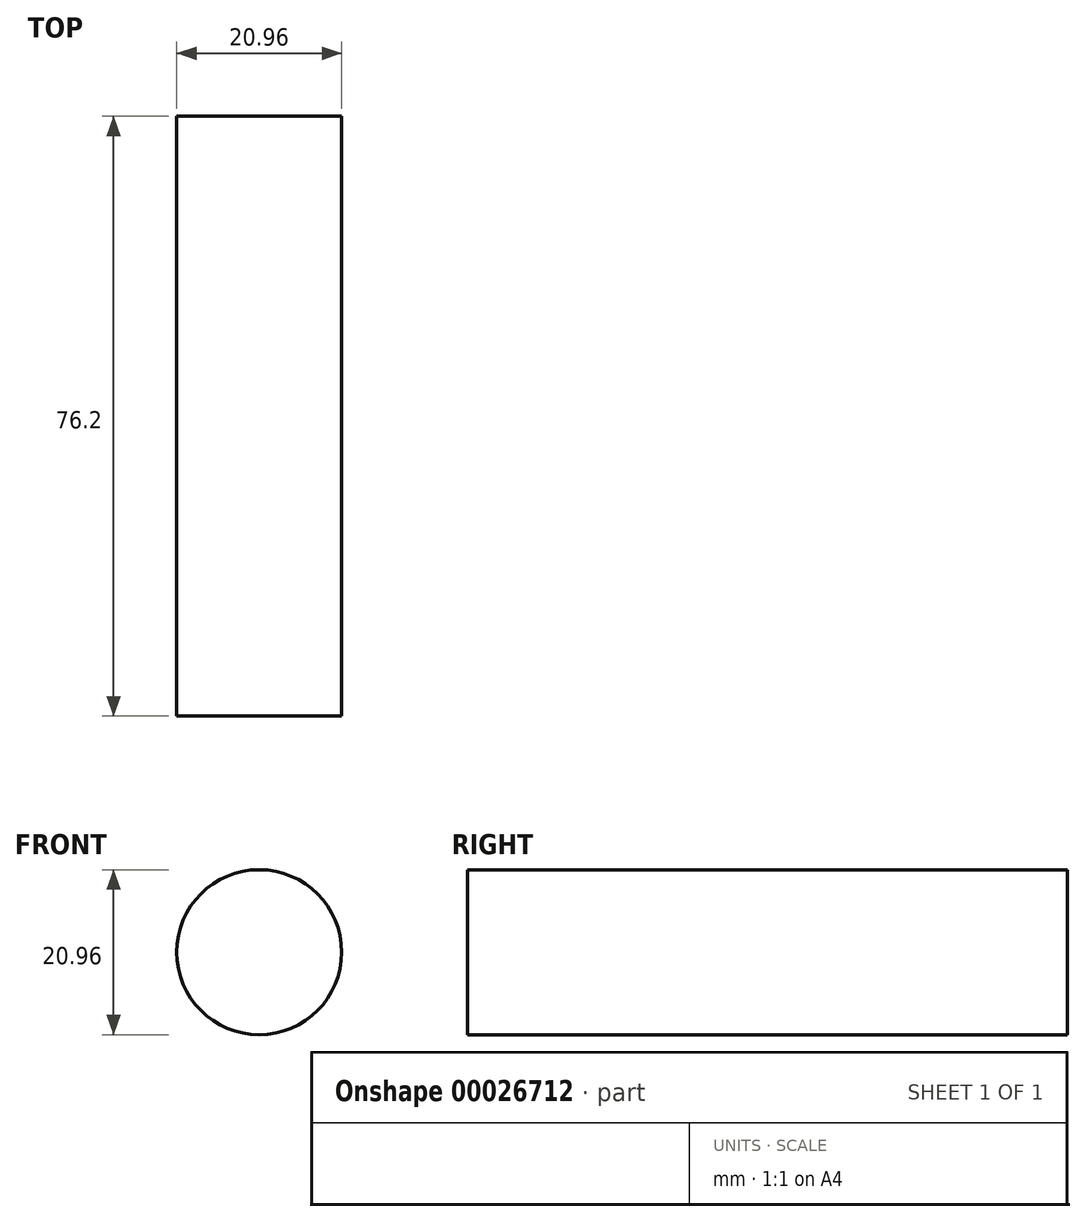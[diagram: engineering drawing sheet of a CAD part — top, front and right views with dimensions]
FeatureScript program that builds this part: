
annotation { "Feature Type Name" : "Feature", "Feature Type Description" : "" }
export const myFeature = defineFeature(function(context is Context, id is Id, definition is map)
    precondition{}
    {
        {
            var Q0;
            Q0=qCreatedBy(makeId("Front.planeOp"),FACE);
            var sketch = newSketch(context, id + "F0", { "sketchPlane" : qUnion([Q0])});
            skCircle(sketch, "E0", {"center": v(-27.27, 28.09) * mm, "radius": 10.48 * mm});
            skSolve(sketch);
        }
        {
            var Q0;
            Q0=makeQuery(id+"F0.imprint","IMPRINT",FACE,{"disambiguationData":[TD([[makeQuery(id+"F0.imprint","IMPRINT",EDGE,{"derivedFrom":sQuery(id+"F0.wireOp",EDGE,"E0")}),1.0]])]});
            extrude(context, id + "F1", {"entities" : qUnion([Q0]), "depth" : 76.2 * mm});
        }
    });
